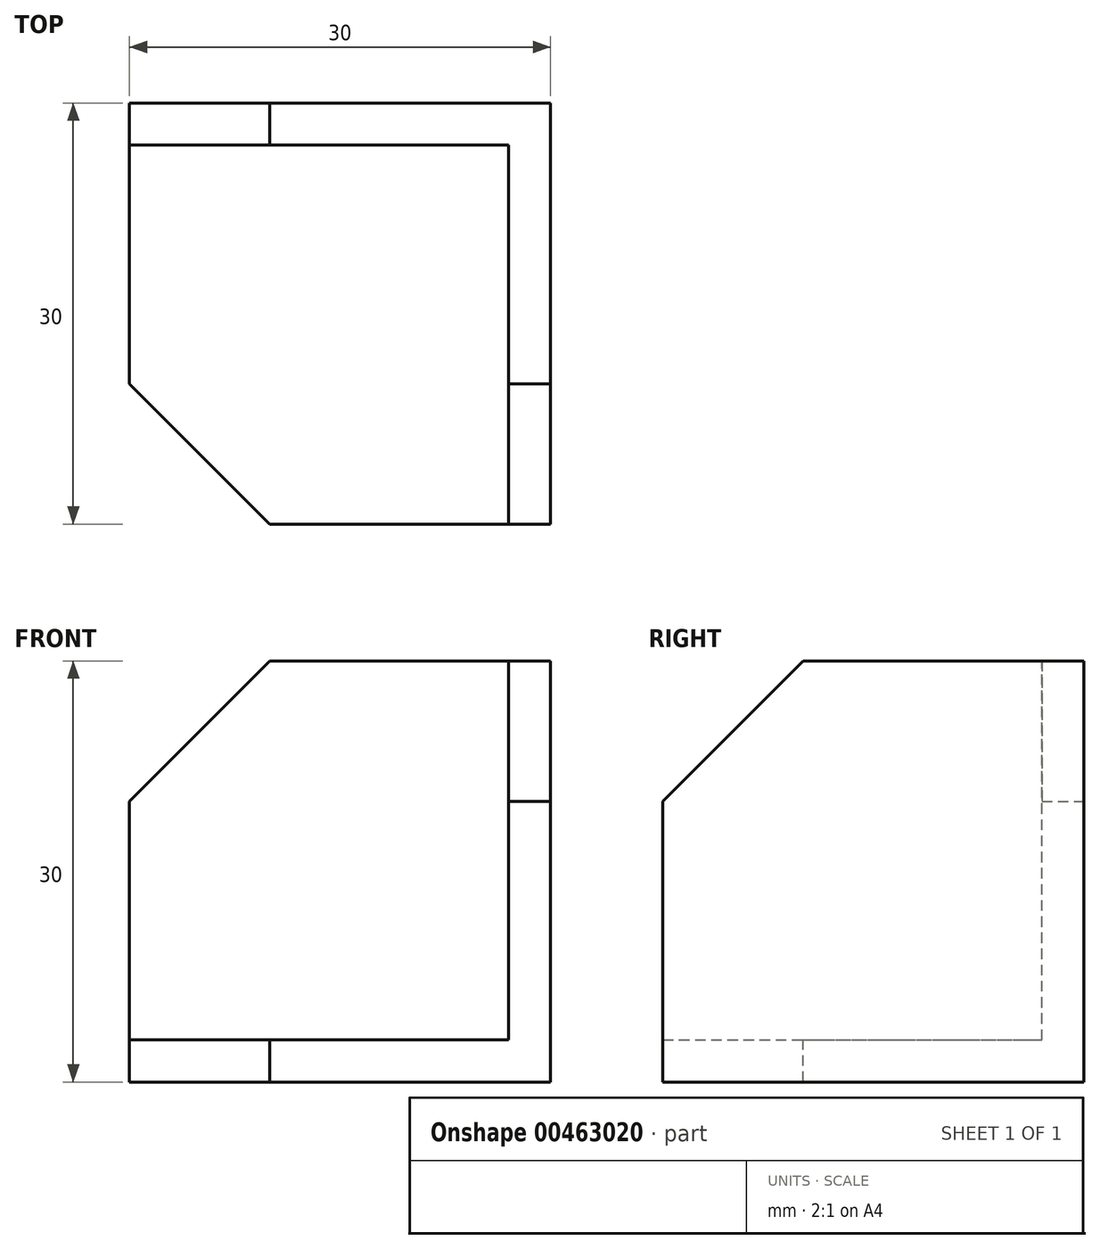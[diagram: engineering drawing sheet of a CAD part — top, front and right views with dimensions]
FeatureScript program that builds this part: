
annotation { "Feature Type Name" : "Feature", "Feature Type Description" : "" }
export const myFeature = defineFeature(function(context is Context, id is Id, definition is map)
    precondition{}
    {
        {
            var Q0;
            Q0=qCreatedBy(makeId("Top.planeOp"),FACE);
            var sketch = newSketch(context, id + "F0", { "sketchPlane" : qUnion([Q0])});
            skLineSegment(sketch, "E0.bottom", {"start": v(0, 0) * mm, "end": v(30, 0) * mm});
            skLineSegment(sketch, "E0.top", {"start": v(0, 30) * mm, "end": v(30, 30) * mm});
            skLineSegment(sketch, "E0.left", {"start": v(0, 0) * mm, "end": v(0, 30) * mm});
            skLineSegment(sketch, "E0.right", {"start": v(30, 0) * mm, "end": v(30, 30) * mm});
            skSolve(sketch);
        }
        {
            var Q0;
            Q0 = qSketchRegion(id + "F0", true);
            extrude(context, id + "F1", {"entities" : qUnion([Q0]), "depth" : 30 * mm});
        }
        {
            var Q0;
            Q0=makeQuery(id+"F1.opExtrude","SWEPT_EDGE",EDGE,{"disambiguationData":[OSD([sQuery(id+"F0.wireOp",EDGE,"E0.bottom"),sQuery(id+"F0.wireOp",EDGE,"E0.left")])]});
            chamfer(context, id + "F2", {"entities" : qUnion([Q0]), "width" : 10 * mm, "tangentPropagation" : true});
        }
        {
            var Q0;
            Q0=makeQuery(id+"F1.opExtrude","CAP_EDGE",EDGE,{"disambiguationData":[OSD([sQuery(id+"F0.wireOp",EDGE,"E0.bottom")])],"isStart":false});
            var Q1;
            {var subQ0=sQuery(id+"F0.wireOp",EDGE,"E0.left");var subQ1=sQuery(id+"F0.wireOp",EDGE,"E0.bottom");Q1=makeQuery(id+"F2.opChamfer","BLEND_EDGE",EDGE,{"blendedFrom":[makeQuery(id+"F1.opExtrude","SWEPT_EDGE",EDGE,{"disambiguationData":[OSD([subQ1,subQ0])]}),makeQuery(id+"F1.opExtrude","CAP_FACE",FACE,{"disambiguationData":[OSD([subQ1,sQuery(id+"F0.wireOp",EDGE,"E0.top"),subQ0,sQuery(id+"F0.wireOp",EDGE,"E0.right")])],"isStart":false})],"blendedInto":[makeQuery(id+"F1.opExtrude","CAP_FACE",FACE,{"disambiguationData":[OSD([subQ1,sQuery(id+"F0.wireOp",EDGE,"E0.top"),subQ0,sQuery(id+"F0.wireOp",EDGE,"E0.right")])],"isStart":false})]});}
            var Q2;
            Q2=makeQuery(id+"F1.opExtrude","CAP_EDGE",EDGE,{"disambiguationData":[OSD([sQuery(id+"F0.wireOp",EDGE,"E0.left")])],"isStart":false});
            chamfer(context, id + "F3", {"entities" : qUnion([Q0, Q1, Q2]), "width" : 10 * mm, "tangentPropagation" : true});
        }
        {
            var Q0;
            Q0=makeQuery(id+"F1.opExtrude","CAP_FACE",FACE,{"disambiguationData":[OSD([sQuery(id+"F0.wireOp",EDGE,"E0.bottom"),sQuery(id+"F0.wireOp",EDGE,"E0.top"),sQuery(id+"F0.wireOp",EDGE,"E0.left"),sQuery(id+"F0.wireOp",EDGE,"E0.right")])],"isStart":false});
            var sketch = newSketch(context, id + "F4", { "sketchPlane" : qUnion([Q0])});
            skLineSegment(sketch, "E1.0", {"start": v(0, 27) * mm, "end": v(27, 27) * mm});
            skLineSegment(sketch, "E1.1", {"start": v(27, 0) * mm, "end": v(27, 27) * mm});
            skArc(sketch, "E2", {"start": v(0, 27) * mm, "mid": v(-6.82, -6.82) * mm, "end": v(27, 0) * mm});
            skSolve(sketch);
        }
        {
            var Q0;
            Q0 = qSketchRegion(id + "F4", true);
            extrude(context, id + "F5", {"entities" : qUnion([Q0]), "operationType" : NewBodyOperationType.REMOVE, "oppositeDirection" : true, "depth" : 27 * mm});
        }
    });
